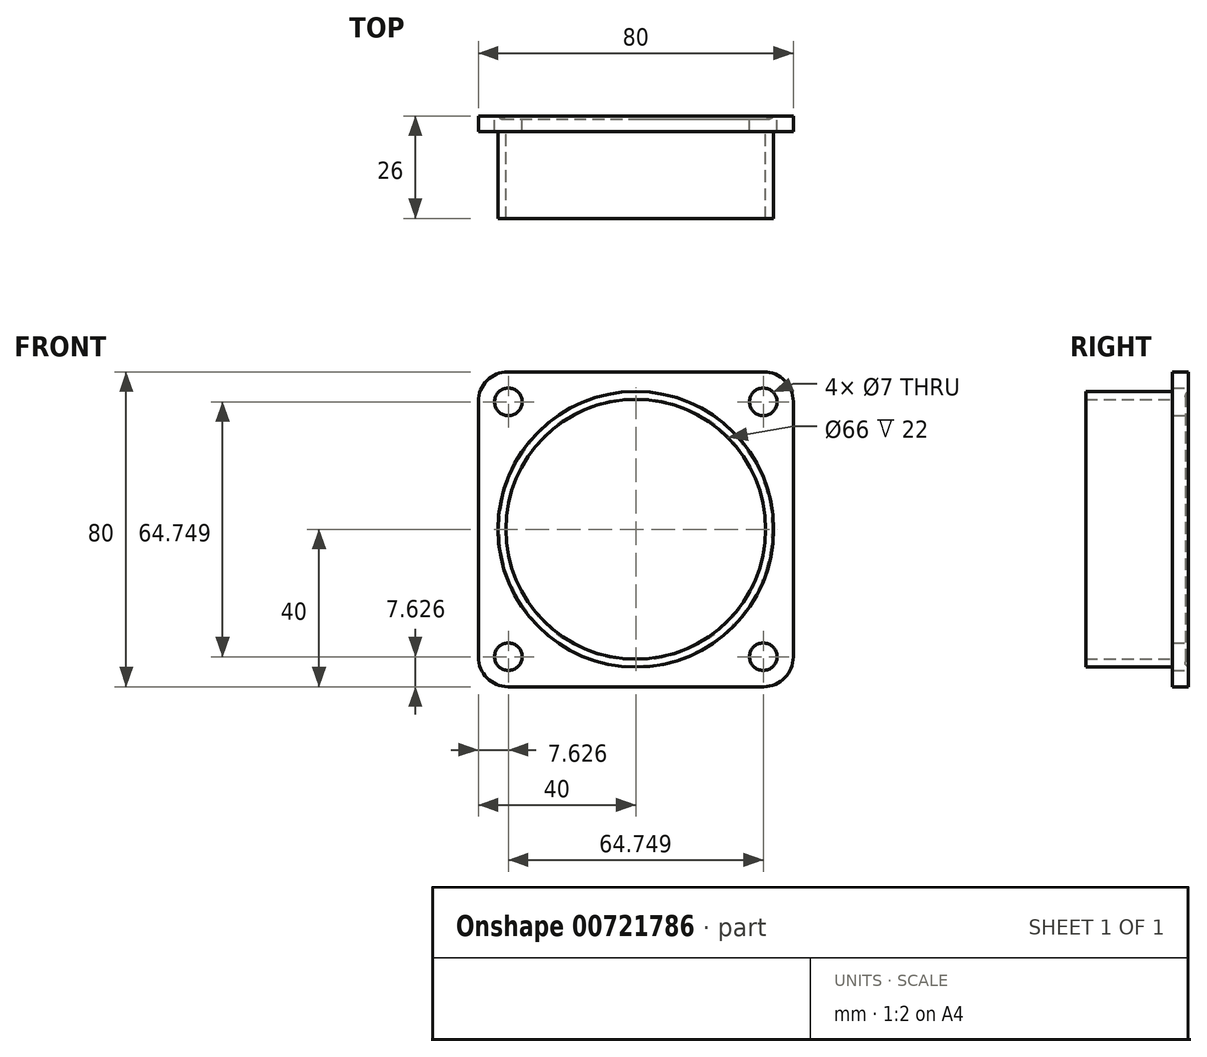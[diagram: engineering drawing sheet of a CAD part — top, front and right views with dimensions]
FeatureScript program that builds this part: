
annotation { "Feature Type Name" : "Feature", "Feature Type Description" : "" }
export const myFeature = defineFeature(function(context is Context, id is Id, definition is map)
    precondition{}
    {
        {
            var Q0;
            Q0=qCreatedBy(makeId("Front.planeOp"),FACE);
            var sketch = newSketch(context, id + "F0", { "sketchPlane" : qUnion([Q0])});
            skLineSegment(sketch, "E0.bottom", {"start": v(-32.5, 40) * mm, "end": v(32.5, 40) * mm});
            skLineSegment(sketch, "E0.top", {"start": v(-32.5, -40) * mm, "end": v(32.5, -40) * mm});
            skLineSegment(sketch, "E0.left", {"start": v(-40, 32.5) * mm, "end": v(-40, -32.5) * mm});
            skLineSegment(sketch, "E0.right", {"start": v(40, 32.5) * mm, "end": v(40, -32.5) * mm});
            skPoint(sketch, "E1", {"position": v(40, 0) * mm});
            skPoint(sketch, "E2", {"position": v(-40, 0) * mm});
            skPoint(sketch, "E3", {"position": v(0, 40) * mm});
            skPoint(sketch, "E4", {"position": v(0, -40) * mm});
            skLineSegment(sketch, "E5", {"start": v(-40, 40) * mm, "end": v(40, -40) * mm, "construction": true});
            skLineSegment(sketch, "E6", {"start": v(40, 40) * mm, "end": v(-40, -40) * mm, "construction": true});
            skPoint(sketch, "E7.visualSharp", {"position": v(-40, 40) * mm});
            skArc(sketch, "E7.filletArc", {"start": v(-32.5, 40) * mm, "mid": v(-37.8, 37.8) * mm, "end": v(-40, 32.5) * mm});
            skPoint(sketch, "E8.visualSharp", {"position": v(40, 40) * mm});
            skArc(sketch, "E8.filletArc", {"start": v(40, 32.5) * mm, "mid": v(37.8, 37.8) * mm, "end": v(32.5, 40) * mm});
            skPoint(sketch, "E9.visualSharp", {"position": v(-40, -40) * mm});
            skArc(sketch, "E9.filletArc", {"start": v(-40, -32.5) * mm, "mid": v(-37.8, -37.8) * mm, "end": v(-32.5, -40) * mm});
            skPoint(sketch, "E10.visualSharp", {"position": v(40, -40) * mm});
            skArc(sketch, "E10.filletArc", {"start": v(32.5, -40) * mm, "mid": v(37.8, -37.8) * mm, "end": v(40, -32.5) * mm});
            skLineSegment(sketch, "E11", {"start": v(0, 40) * mm, "end": v(0, -40) * mm, "construction": true});
            skLineSegment(sketch, "E12", {"start": v(-40, 0) * mm, "end": v(40, 0) * mm, "construction": true});
            skSolve(sketch);
        }
        {
            var Q0;
            Q0=makeQuery(id+"F0.imprint","IMPRINT",FACE,{"disambiguationData":[TD([[makeQuery(id+"F0.imprint","IMPRINT",EDGE,{"derivedFrom":sQuery(id+"F0.wireOp",EDGE,"E0.bottom")}),-1.0]])]});
            var sketch = newSketch(context, id + "F1", { "sketchPlane" : qUnion([Q0])});
            skCircle(sketch, "E13", {"center": v(0, 0) * mm, "radius": 35 * mm});
            skPoint(sketch, "E14", {"position": v(-24.75, 24.75) * mm});
            skLineSegment(sketch, "E15", {"start": v(-24.75, 24.75) * mm, "end": v(-40, 40) * mm, "construction": true});
            skPoint(sketch, "E16", {"position": v(-32.37, 32.37) * mm});
            skCircle(sketch, "E17", {"center": v(0, 0) * mm, "radius": 33 * mm});
            skPoint(sketch, "E18", {"position": v(0, 33) * mm});
            skPoint(sketch, "E19", {"position": v(0, 35) * mm});
            skLineSegment(sketch, "E20", {"start": v(0, 35) * mm, "end": v(0, 33) * mm, "construction": true});
            skPoint(sketch, "E21", {"position": v(0, 34) * mm});
            skSolve(sketch);
        }
        {
            var Q0;
            Q0=makeQuery(id+"F0.imprint","IMPRINT",FACE,{"disambiguationData":[TD([[makeQuery(id+"F0.imprint","IMPRINT",EDGE,{"derivedFrom":sQuery(id+"F0.wireOp",EDGE,"E0.bottom")}),-1.0]])]});
            var sketch = newSketch(context, id + "F2", { "sketchPlane" : qUnion([Q0])});
            skCircle(sketch, "E22", {"center": v(-32.37, 32.37) * mm, "radius": 3.5 * mm});
            skCircle(sketch, "E23.1.0", {"center": v(-32.37, -32.37) * mm, "radius": 3.5 * mm});
            skCircle(sketch, "E23.2.0", {"center": v(32.37, -32.37) * mm, "radius": 3.5 * mm});
            skCircle(sketch, "E23.3.0", {"center": v(32.37, 32.37) * mm, "radius": 3.5 * mm});
            skPoint(sketch, "E23.center", {"position": v(0, 0) * mm});
            skSolve(sketch);
        }
        {
            var Q0;
            Q0 = qSketchRegion(id + "F0", true);
            extrude(context, id + "F3", {"entities" : qUnion([Q0]), "depth" : 4 * mm, "offsetDistance" : 25 * mm});
        }
        {
            var Q0;
            Q0 = qSketchRegion(id + "F1", true);
            extrude(context, id + "F4", {"entities" : qUnion([Q0]), "operationType" : NewBodyOperationType.ADD, "depth" : 26 * mm, "offsetDistance" : 25 * mm});
        }
        {
            var Q0;
            Q0 = qSketchRegion(id + "F2", true);
            extrude(context, id + "F5", {"entities" : qUnion([Q0]), "operationType" : NewBodyOperationType.REMOVE, "endBound" : BoundingType.THROUGH_ALL, "depth" : 25 * mm, "offsetDistance" : 25 * mm});
        }
        {
            var Q0;
            Q0=makeQuery(id+"F4.opExtrude","CAP_FACE",FACE,{"disambiguationData":[OSD([sQuery(id+"F1.wireOp",EDGE,"E13")])],"isStart":false});
            var sketch = newSketch(context, id + "F6", { "sketchPlane" : qUnion([Q0])});
            skCircle(sketch, "E24", {"center": v(0, 0) * mm, "radius": 33 * mm});
            skSolve(sketch);
        }
        {
            var Q0;
            Q0 = qSketchRegion(id + "F6", true);
            extrude(context, id + "F7", {"entities" : qUnion([Q0]), "operationType" : NewBodyOperationType.REMOVE, "oppositeDirection" : true, "depth" : 22 * mm, "offsetDistance" : 25 * mm});
        }
        {
            var Q0;
            Q0=qCreatedBy(makeId("Right.planeOp"),FACE);
            var sketch = newSketch(context, id + "F8", { "sketchPlane" : qUnion([Q0])});
            skCircle(sketch, "E25", {"center": v(0, 34) * mm, "radius": 0.75 * mm});
            skSolve(sketch);
        }
        {
            var Q0;
            Q0=makeQuery(id+"F8.imprint","IMPRINT",FACE,{"disambiguationData":[TD([[makeQuery(id+"F8.imprint","IMPRINT",EDGE,{"derivedFrom":sQuery(id+"F8.wireOp",EDGE,"E25")}),1.0]])]});
            var Q1;
            Q1=sQuery(id+"F1.wireOp",EDGE,"E17");
            sweep(context, id + "F9", {"operationType" : NewBodyOperationType.REMOVE, "profiles" : qUnion([Q0]), "path" : qUnion([Q1])});
        }
    });
